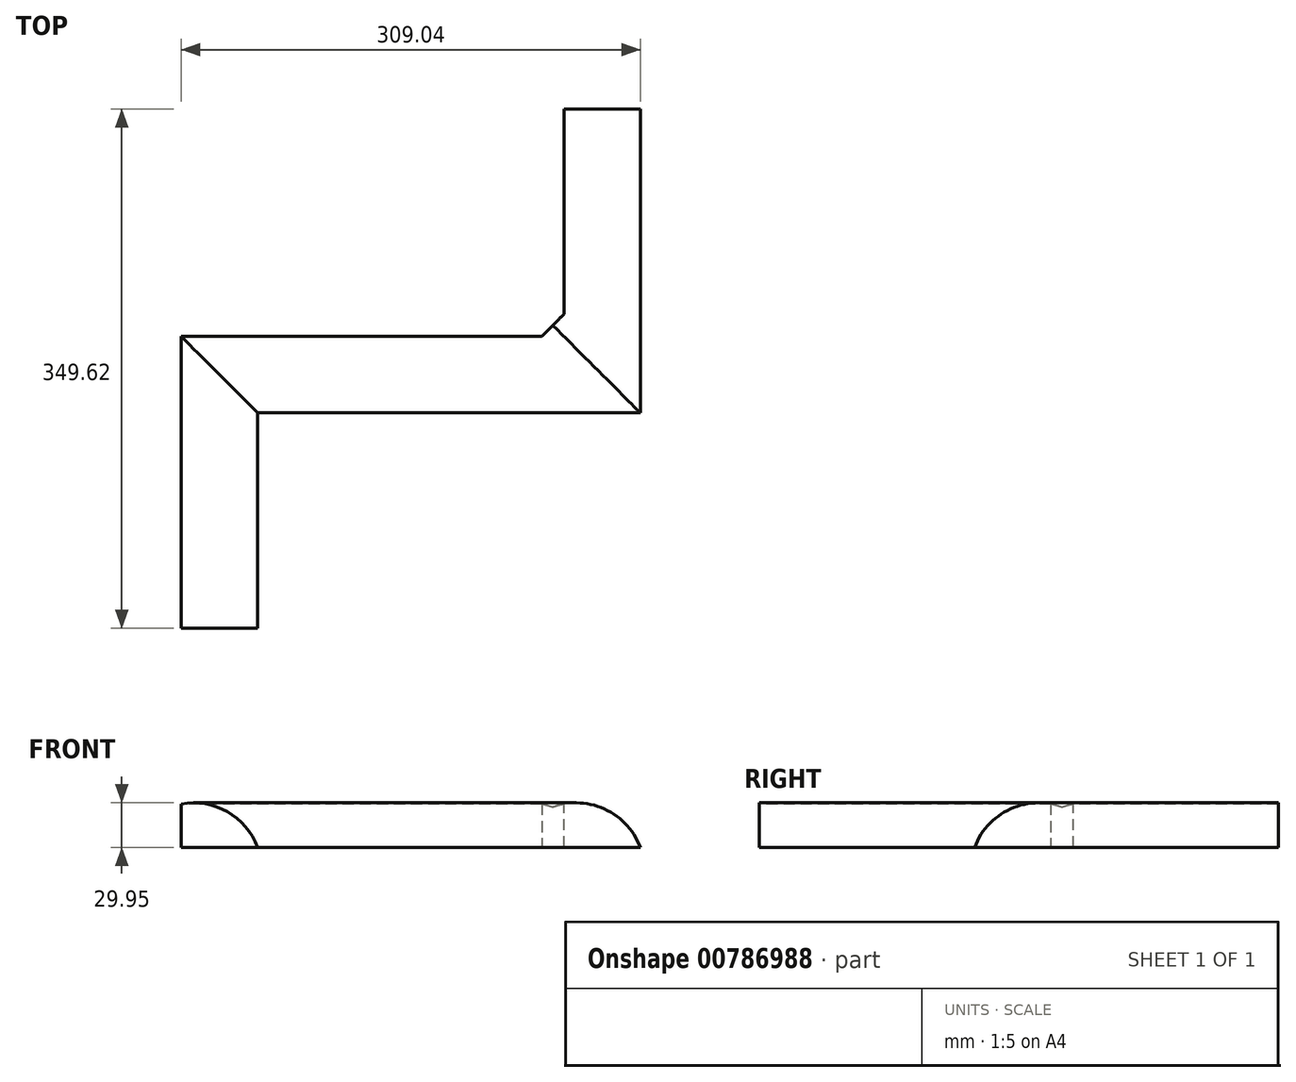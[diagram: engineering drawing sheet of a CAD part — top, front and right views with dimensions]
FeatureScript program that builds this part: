
annotation { "Feature Type Name" : "Feature", "Feature Type Description" : "" }
export const myFeature = defineFeature(function(context is Context, id is Id, definition is map)
    precondition{}
    {
        {
            var Q0;
            Q0=qCreatedBy(makeId("Front.planeOp"),FACE);
            var sketch = newSketch(context, id + "F0", { "sketchPlane" : qUnion([Q0])});
            skEllipse(sketch, "E0", {"center": v(0, 0) * mm, "majorRadius": 44.37 * mm, "minorRadius": 22.19 * mm, "majorAxis": v(-1, 0)});
            skLineSegment(sketch, "E1", {"start": v(-44.37, 0) * mm, "end": v(44.37, 0) * mm, "construction": true});
            skLineSegment(sketch, "E2", {"start": v(0, -22.19) * mm, "end": v(0, 22.19) * mm, "construction": true});
            skPoint(sketch, "E3", {"position": v(0, 29.19) * mm});
            skPoint(sketch, "E4", {"position": v(51.37, 0) * mm});
            skArc(sketch, "E5", {"start": v(51.37, 0) * mm, "mid": v(31.01, 23.97) * mm, "end": v(0, 29.19) * mm});
            skLineSegment(sketch, "E6", {"start": v(0, 29.19) * mm, "end": v(0, 0) * mm});
            skLineSegment(sketch, "E7", {"start": v(51.37, 0) * mm, "end": v(0, 0) * mm});
            skSolve(sketch);
        }
        {
            var Q0;
            Q0=qCreatedBy(makeId("Top.planeOp"),FACE);
            var sketch = newSketch(context, id + "F1", { "sketchPlane" : qUnion([Q0])});
            skLineSegment(sketch, "E8", {"start": v(0, 0) * mm, "end": v(0, -153.1) * mm});
            skLineSegment(sketch, "E9", {"start": v(0, -153.1) * mm, "end": v(-257.67, -153.1) * mm});
            skLineSegment(sketch, "E10", {"start": v(-257.67, -153.1) * mm, "end": v(-257.67, -349.62) * mm});
            skSolve(sketch);
        }
        {
            var Q0;
            {var subQ0=sQuery(id+"F0.wireOp",EDGE,"E6");var subQ1=sQuery(id+"F0.wireOp",EDGE,"E0");var subQ2=makeQuery(id+"F0.imprint","INTERSECT",VERTEX,{"derivedFrom":[subQ1,subQ0]});Q0=makeQuery(id+"F0.imprint","IMPRINT",FACE,{"disambiguationData":[TD([[makeQuery(id+"F0.imprint","IMPRINT",EDGE,{"disambiguationData":[TD([[subQ2,1.0]])],"derivedFrom":subQ1}),1.0]])]});}
            var Q1;
            {var subQ5=sQuery(id+"F0.wireOp",EDGE,"E5");Q1=makeQuery(id+"F0.imprint","IMPRINT",FACE,{"disambiguationData":[TD([[makeQuery(id+"F0.imprint","IMPRINT",EDGE,{"derivedFrom":subQ5}),1.0]])]});}
            var Q2;
            Q2=sQuery(id+"F0.wireOp",EDGE,"E5");
            var Q3;
            Q3=sQuery(id+"F0.wireOp",EDGE,"E6");
            var Q4;
            Q4=sQuery(id+"F0.wireOp",EDGE,"E7");
            var Q5;
            Q5=sQuery(id+"F1.wireOp",EDGE,"E8");
            var Q6;
            Q6=sQuery(id+"F1.wireOp",EDGE,"E9");
            var Q7;
            Q7=sQuery(id+"F1.wireOp",EDGE,"E10");
            sweep(context, id + "F2", {"profiles" : qUnion([Q0, Q1]), "surfaceProfiles" : qUnion([Q2, Q3, Q4]), "path" : qUnion([Q5, Q6, Q7])});
        }
        {
            var Q0;
            Q0=makeQuery(id+"F2.opSweep","MID_CAP_EDGE",EDGE,{"disambiguationData":[OSD([sQuery(id+"F0.wireOp",EDGE,"E6"),sQuery(id+"F1.wireOp",VERTEX,"E9.start")])],"capPos":1.0});
            chamfer(context, id + "F3", {"entities" : qUnion([Q0]), "chamferType" : ChamferType.TWO_OFFSETS, "width1" : 15 * mm, "oppositeDirection" : false, "width2" : 15 * mm, "tangentPropagation" : true});
        }
    });
